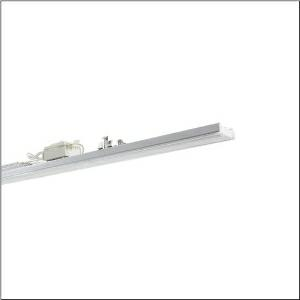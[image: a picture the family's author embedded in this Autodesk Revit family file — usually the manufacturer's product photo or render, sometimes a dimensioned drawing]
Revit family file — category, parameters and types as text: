
# Revit family: licross_r__11_recessed_mo_51tl18vn455g_918d
name_source: partatom
category: Lighting Fixtures
units: mm (PartAtom-declared; Revit-internal decimal feet)

## family parameters
Cut with Voids When Loaded = No
Host = Face
Light Source = No
Part Type = Normal
Room Calculation Point = No
Round Connector Dimension = Use Diameter
Shared = No

## types (1)
- --- (1 x LED, 5560 lm, 30 W, 4000K)
    Apparent Load = 30 VA
    CIE Flux Codes = 83 96 99 100 100
    Color Rendering = 80
    Color Temperature = 4000K
    Default Elevation = 1800 mm
    Description = Licross® 11 Recessed MO, luminaire insert, of sheet steel, galvanised, coil coated, white, length: 1.500mm, width: 66mm, height: 67mm, LED rated luminous flux: 5.560lm, light colour: 840, control gear: DALI 2, CLO, with plug, 5-pole, with phase selection, mains connection: 220..240V, AC, 50/60Hz, start of lifetime: 30W, end of service life: 34W, internal wiring halogen-free, primary optical cover: cover, of PMMA, light emission: direct distribution, primary light characteristic: symmetric, protection rating (complete): IP40, insulation class (complete): insulation class I (protective earthing), certification: CE, ENEC, VDE, UKCA, protection symbol: D if used in an environment without relevant dust loads with corresponding accessories, impact resistance: IK06, permissible ambient temperature for indoor applications: -25..+40°C, corresponds to IFS (International Featured Standards) requirements for safety and quality in the food industry, reducing of maximum allowable ambient temperature of 5°C with ceiling mounting, LABS conformity tested according to VDMA 24364:2018-05, packaging unit: 1 piece
    Height = 58 mm
    Lamp = 1 x LED
    Lamp Light Flux = 5560 lm
    Lamp Power = 30 W
    Lamp count = 1
    Length = 1500 mm
    Luminous efficacy = 185 lm/W
    Manufacturer = Siteco
    ModVariant = No
    Model = 51TL18VN455G
    Mounting Place = Ceiling
    Mounting Type = Pendant
    Number of Poles = 1
    OnlyDefault = Yes
    Power Factor = 1
    Product Name = Licross® 11 Recessed MO
    Product group = luminaire insert | ceiling pendant
    ProductGroupID = 902
    Protection Class = Protection class I
    Protection Degree = IP 40
    RLX_Detail_Level = 1
    RLX_Emergency_Light_Flux = 0 lm
    RLX_Emergency_Type = 0
    RLX_Emergency_Type_DB = No
    RlxData = <blob elided: 24105 chars, md5=fa739211>
    Socket = socket
    Standby Power = 0 W
    System Light Flux = 5560 lm
    System Power = 30 W
    Type Comments = factory setting: luminous flux: 100 % | dim-lin: 254 | 203 mA
    Type Image = l_1296930.jpg
    URL = http://relux.com
    VarID = @adj_069497
    Voltage = 0 V
    Weight = 0.00 kg
    Width = 66 mm

## geometry (parser evidence)
native form markers: Blend x4, Sweep x11
no freeform markers — native parametric forms only
